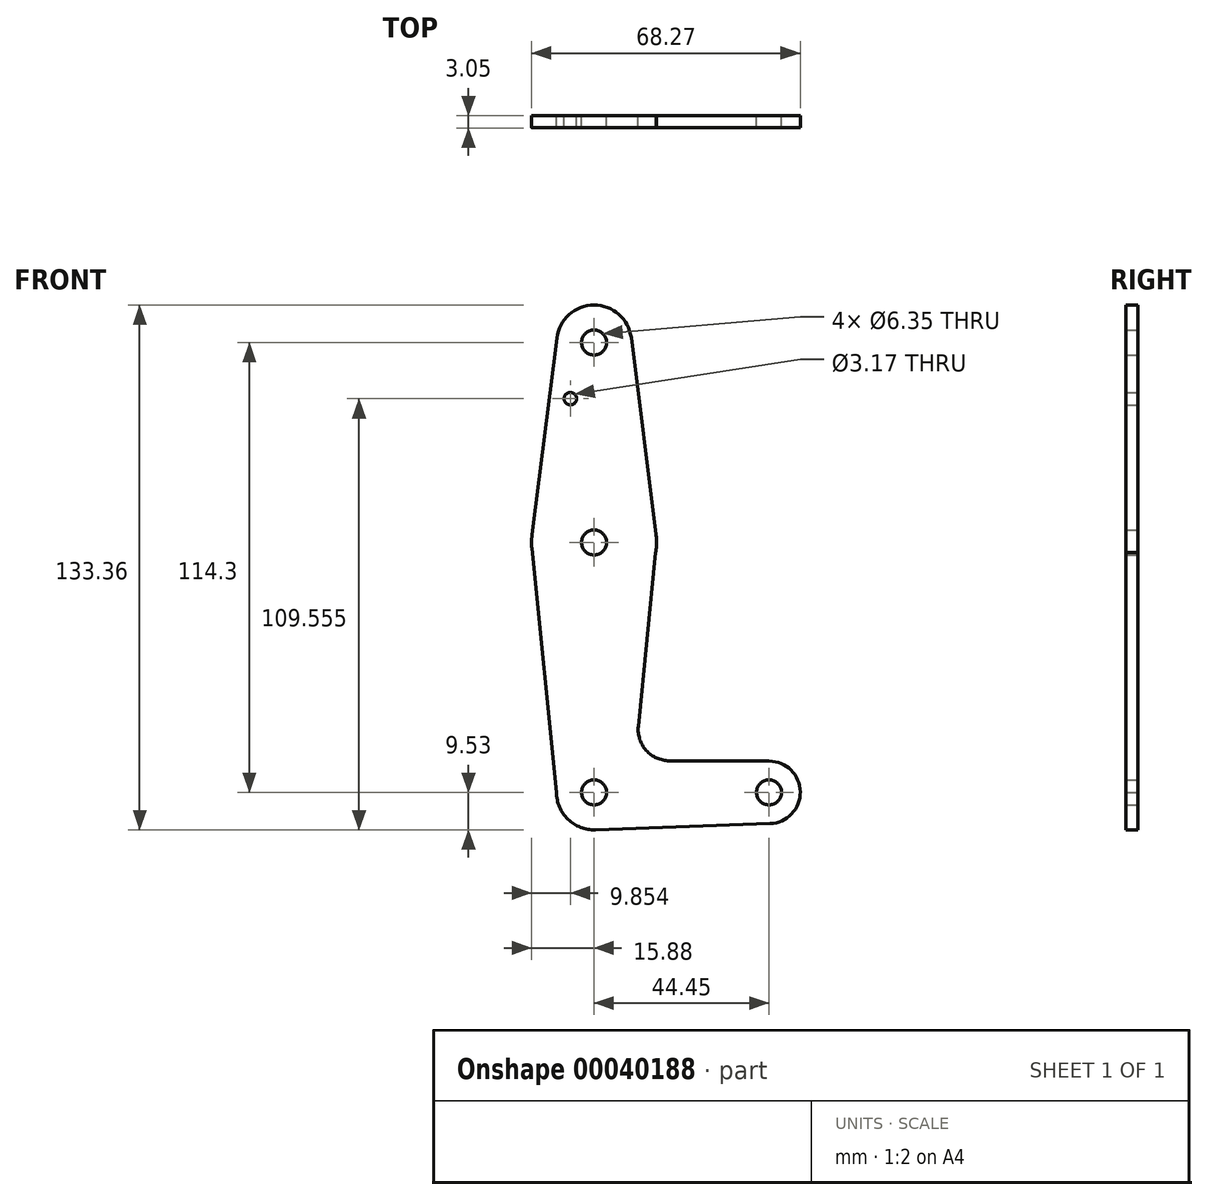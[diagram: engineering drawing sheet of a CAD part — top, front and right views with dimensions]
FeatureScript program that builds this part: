
annotation { "Feature Type Name" : "Feature", "Feature Type Description" : "" }
export const myFeature = defineFeature(function(context is Context, id is Id, definition is map)
    precondition{}
    {
        {
            var Q0;
            Q0=qCreatedBy(makeId("Front.planeOp"),FACE);
            var sketch = newSketch(context, id + "F0", { "sketchPlane" : qUnion([Q0])});
            skLineSegment(sketch, "E0", {"start": v(0, 0) * mm, "end": v(0, 63.5) * mm, "construction": true});
            skLineSegment(sketch, "E1", {"start": v(0, 63.5) * mm, "end": v(0, 114.3) * mm, "construction": true});
            skLineSegment(sketch, "E2", {"start": v(0, 0) * mm, "end": v(44.45, 0) * mm, "construction": true});
            skCircle(sketch, "E3", {"center": v(0, 114.3) * mm, "radius": 9.53 * mm});
            skCircle(sketch, "E4", {"center": v(0, 63.5) * mm, "radius": 15.88 * mm});
            skCircle(sketch, "E5", {"center": v(0, 0) * mm, "radius": 9.53 * mm});
            skCircle(sketch, "E6", {"center": v(44.45, 0) * mm, "radius": 7.94 * mm});
            skLineSegment(sketch, "E7", {"start": v(-9.52, 0) * mm, "end": v(-15.8, 61.9) * mm});
            skLineSegment(sketch, "E8", {"start": v(15.75, 65.48) * mm, "end": v(9.45, 115.5) * mm});
            skLineSegment(sketch, "E9", {"start": v(-15.75, 65.48) * mm, "end": v(-9.46, 115.42) * mm});
            skLineSegment(sketch, "E10", {"start": v(44.73, -7.93) * mm, "end": v(0.34, -9.52) * mm});
            skCircle(sketch, "E11", {"center": v(0, 0) * mm, "radius": 3.18 * mm});
            skCircle(sketch, "E12", {"center": v(0, 63.5) * mm, "radius": 3.18 * mm});
            skCircle(sketch, "E13", {"center": v(0, 114.3) * mm, "radius": 3.18 * mm});
            skCircle(sketch, "E14", {"center": v(44.45, 0) * mm, "radius": 3.18 * mm});
            skCircle(sketch, "E15", {"center": v(-6.03, 100.03) * mm, "radius": 1.59 * mm});
            skPoint(sketch, "E16.start.orphan", {"position": v(44.73, 7.93) * mm});
            skLineSegment(sketch, "E17", {"start": v(15.86, 62.91) * mm, "end": v(11.25, 16.77) * mm});
            skLineSegment(sketch, "E18", {"start": v(9.48, -0.95) * mm, "end": v(10.6, -1.66) * mm});
            skLineSegment(sketch, "E19", {"start": v(19.13, 8.03) * mm, "end": v(45.82, 7.93) * mm});
            skLineSegment(sketch, "E20", {"start": v(45.82, 7.93) * mm, "end": v(46.48, 9.7) * mm});
            skPoint(sketch, "E21.newPointA", {"position": v(0, 8.1) * mm});
            skArc(sketch, "E21.filletArc", {"start": v(11.25, 16.77) * mm, "mid": v(13.26, 10.66) * mm, "end": v(19.13, 8.03) * mm});
            skSolve(sketch);
        }
        {
            var Q0;
            Q0 = qSketchRegion(id + "F0", true);
            extrude(context, id + "F1", {"entities" : qUnion([Q0]), "depth" : 3.05 * mm});
        }
    });
